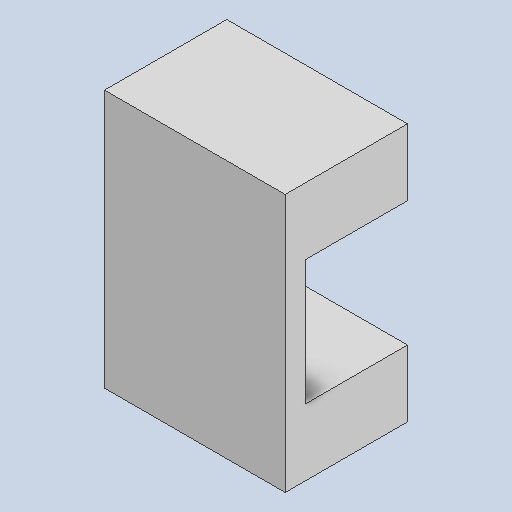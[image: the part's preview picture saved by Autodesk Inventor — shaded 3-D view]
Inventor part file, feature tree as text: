
AUTODESK INVENTOR PART (.ipt)
format: ipt  version: 2022 (Build 260153000, 153)  size: 154,112 bytes
history: native  units: mm
features: other x5, extrude x4, reference x4, sketch x3
ambient origin geometry x8: Origin, YZ Plane, XZ Plane, XY Plane, X Axis, Y Axis, Z Axis, Center Point
bodies: Solid1 (feature_tree)
feature tree (16):
  extrude  "Extrusion1"  Depth=0.3mm
  extrude  "Extrusion3"  Depth=0.3mm
  sketch  "Sketch5"  dims[d4=0.3mm d5=24.4mm d6=3.8mm d7=3.0mm d8=15.0mm d9=0.0mm d12=3.0mm d13=0.0mm d14=4.0mm d15=6.0mm d16=8.0mm d17=9.2mm d18=1.0mm d19=0.0mm d20=80.0mm d21=0.0mm]
  extrude  "Extrusion4"  Depth=24.4mm
  extrude  "Extrusion5"  Depth=3.8mm
  sketch  "Sketch1"  dims[d0=0.3mm d1=0.3mm]
  reference  "Reference1"
  reference  "Reference2"
  reference  "Reference3"
  reference  "Reference4"
  sketch  "Sketch4"  dims[d2=0.3mm d3=0.3mm]
  other  "<userpath>\OneDrive\Escritorio\Mini_Proyecto_Diseno\Diseno_18012\Modelo_MPD\Carril.iam"
  other  "Carril.iam"
  other  "Lateral_Carril:2"
  other  "Lateral_Carril:1"
  other  "Base_Carril:1"
